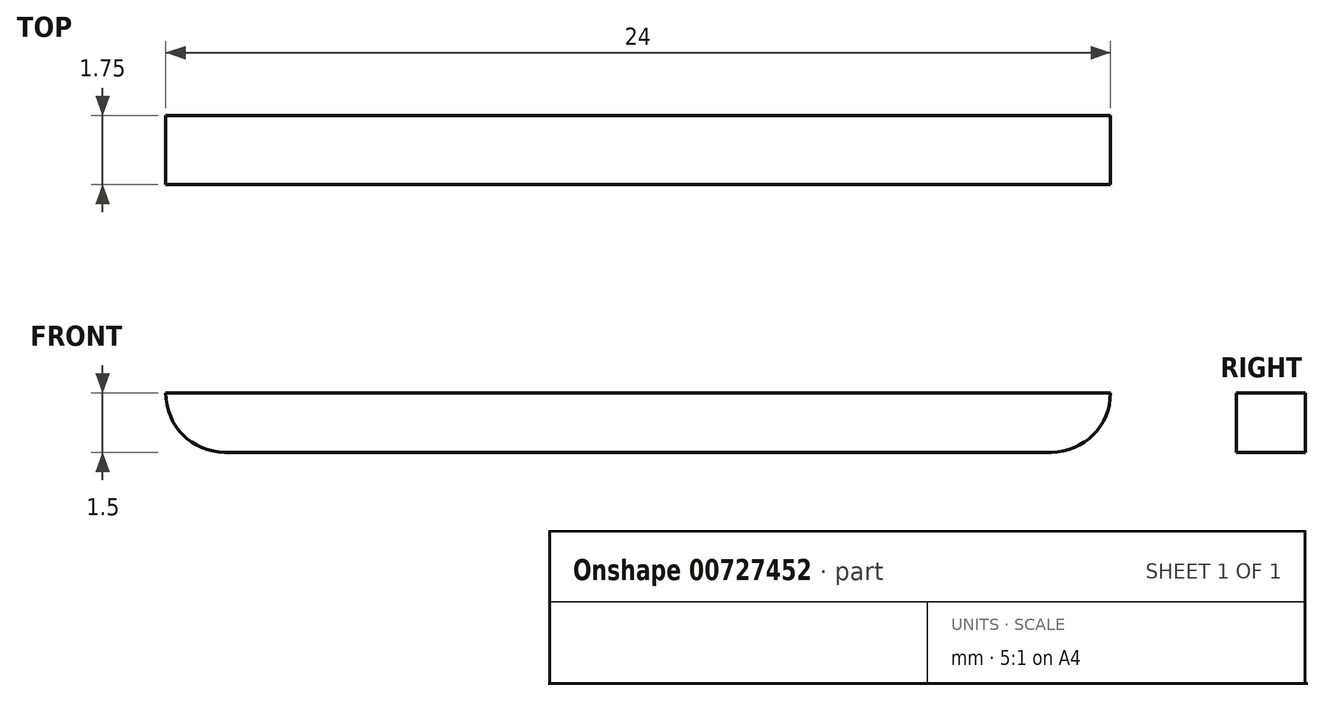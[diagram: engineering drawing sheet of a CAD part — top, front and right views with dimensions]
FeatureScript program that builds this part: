
annotation { "Feature Type Name" : "Feature", "Feature Type Description" : "" }
export const myFeature = defineFeature(function(context is Context, id is Id, definition is map)
    precondition{}
    {
        {
            var Q0;
            Q0=qCreatedBy(makeId("Front.planeOp"),FACE);
            var sketch = newSketch(context, id + "F0", { "sketchPlane" : qUnion([Q0])});
            skArc(sketch, "E0", {"start": v(-12, 0.75) * mm, "mid": v(-11.56, -0.31) * mm, "end": v(-10.5, -0.75) * mm});
            skArc(sketch, "E1", {"start": v(10.5, -0.75) * mm, "mid": v(11.56, -0.31) * mm, "end": v(12, 0.75) * mm});
            skLineSegment(sketch, "E2", {"start": v(-10.5, -0.75) * mm, "end": v(10.5, -0.75) * mm});
            skLineSegment(sketch, "E3", {"start": v(-12, 0.75) * mm, "end": v(12, 0.75) * mm});
            skSolve(sketch);
        }
        {
            var Q0;
            Q0 = qSketchRegion(id + "F0", true);
            extrude(context, id + "F1", {"entities" : qUnion([Q0]), "depth" : 1.75 * mm, "offsetDistance" : 25 * mm});
        }
    });
